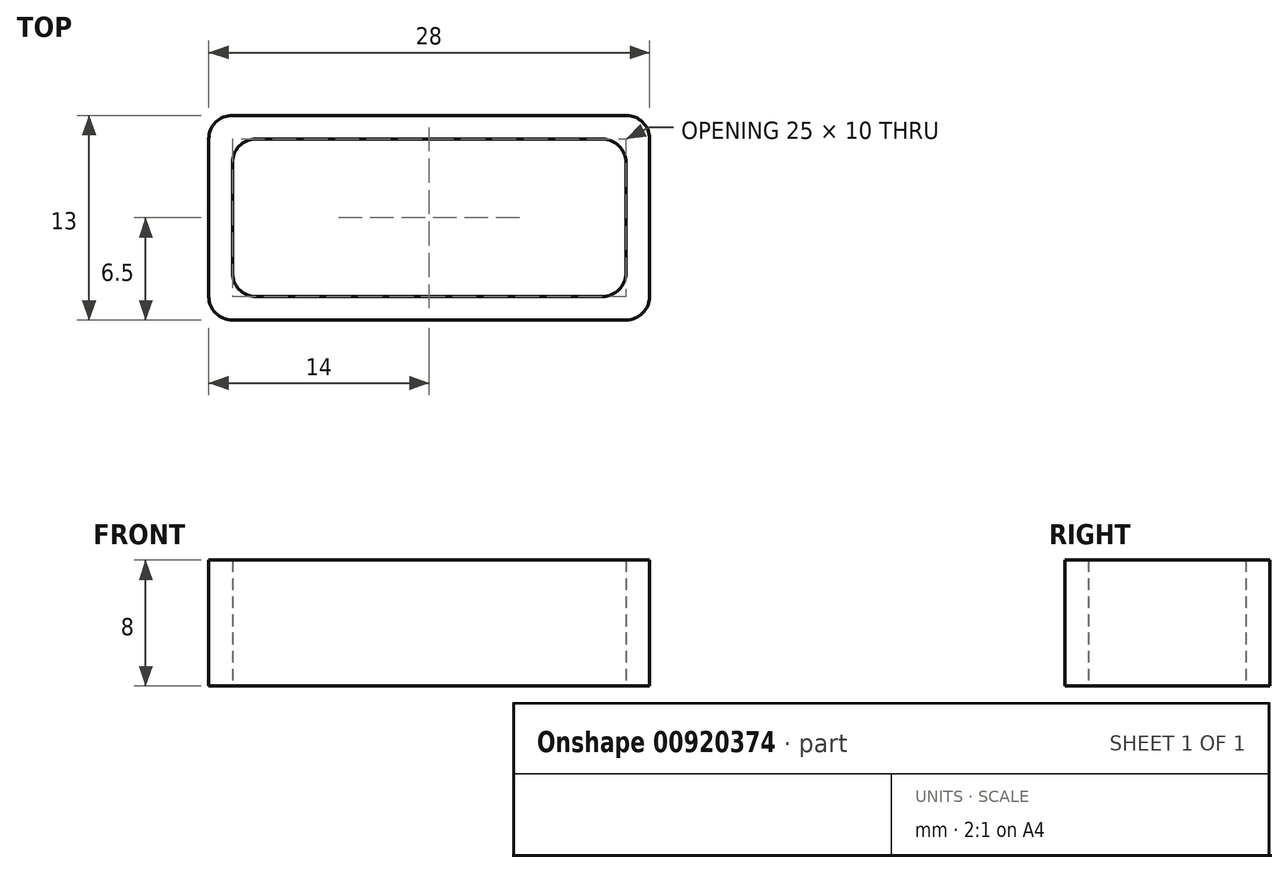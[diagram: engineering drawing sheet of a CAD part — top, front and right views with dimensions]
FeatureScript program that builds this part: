
annotation { "Feature Type Name" : "Feature", "Feature Type Description" : "" }
export const myFeature = defineFeature(function(context is Context, id is Id, definition is map)
    precondition{}
    {
        {
            var Q0;
            Q0=qCreatedBy(makeId("Top.planeOp"),FACE);
            var sketch = newSketch(context, id + "F0", { "sketchPlane" : qUnion([Q0])});
            skLineSegment(sketch, "E0.bottom", {"start": v(14, 6.5) * mm, "end": v(-14, 6.5) * mm});
            skLineSegment(sketch, "E0.top", {"start": v(14, -6.5) * mm, "end": v(-14, -6.5) * mm});
            skLineSegment(sketch, "E0.left", {"start": v(14, 6.5) * mm, "end": v(14, -6.5) * mm});
            skLineSegment(sketch, "E0.right", {"start": v(-14, 6.5) * mm, "end": v(-14, -6.5) * mm});
            skPoint(sketch, "E0.middle", {"position": v(0, 0) * mm});
            skLineSegment(sketch, "E1.bottom", {"start": v(12.5, 5) * mm, "end": v(-12.5, 5) * mm});
            skLineSegment(sketch, "E1.top", {"start": v(12.5, -5) * mm, "end": v(-12.5, -5) * mm});
            skLineSegment(sketch, "E1.left", {"start": v(12.5, 5) * mm, "end": v(12.5, -5) * mm});
            skLineSegment(sketch, "E1.right", {"start": v(-12.5, 5) * mm, "end": v(-12.5, -5) * mm});
            skSolve(sketch);
        }
        {
            var Q0;
            Q0=makeQuery(id+"F0.imprint","IMPRINT",FACE,{"disambiguationData":[TD([[makeQuery(id+"F0.imprint","IMPRINT",EDGE,{"derivedFrom":sQuery(id+"F0.wireOp",EDGE,"E0.bottom")}),1.0]])]});
            extrude(context, id + "F1", {"entities" : qUnion([Q0]), "depth" : 8 * mm, "offsetDistance" : 25 * mm});
        }
        {
            var Q0;
            Q0=makeQuery(id+"F1.opExtrude","SWEPT_EDGE",EDGE,{"disambiguationData":[OSD([sQuery(id+"F0.wireOp",EDGE,"E1.bottom"),sQuery(id+"F0.wireOp",EDGE,"E1.left")])]});
            var Q1;
            Q1=makeQuery(id+"F1.opExtrude","SWEPT_EDGE",EDGE,{"disambiguationData":[OSD([sQuery(id+"F0.wireOp",EDGE,"E1.bottom"),sQuery(id+"F0.wireOp",EDGE,"E1.right")])]});
            var Q2;
            Q2=makeQuery(id+"F1.opExtrude","SWEPT_EDGE",EDGE,{"disambiguationData":[OSD([sQuery(id+"F0.wireOp",EDGE,"E1.top"),sQuery(id+"F0.wireOp",EDGE,"E1.left")])]});
            var Q3;
            Q3=makeQuery(id+"F1.opExtrude","SWEPT_EDGE",EDGE,{"disambiguationData":[OSD([sQuery(id+"F0.wireOp",EDGE,"E1.top"),sQuery(id+"F0.wireOp",EDGE,"E1.right")])]});
            var Q4;
            Q4=makeQuery(id+"F1.opExtrude","SWEPT_EDGE",EDGE,{"disambiguationData":[OSD([sQuery(id+"F0.wireOp",EDGE,"E0.bottom"),sQuery(id+"F0.wireOp",EDGE,"E0.left")])]});
            var Q5;
            Q5=makeQuery(id+"F1.opExtrude","SWEPT_EDGE",EDGE,{"disambiguationData":[OSD([sQuery(id+"F0.wireOp",EDGE,"E0.top"),sQuery(id+"F0.wireOp",EDGE,"E0.left")])]});
            var Q6;
            Q6=makeQuery(id+"F1.opExtrude","SWEPT_EDGE",EDGE,{"disambiguationData":[OSD([sQuery(id+"F0.wireOp",EDGE,"E0.bottom"),sQuery(id+"F0.wireOp",EDGE,"E0.right")])]});
            var Q7;
            Q7=makeQuery(id+"F1.opExtrude","SWEPT_EDGE",EDGE,{"disambiguationData":[OSD([sQuery(id+"F0.wireOp",EDGE,"E0.top"),sQuery(id+"F0.wireOp",EDGE,"E0.right")])]});
            fillet(context, id + "F2", {"entities" : qUnion([Q0, Q1, Q2, Q3, Q4, Q5, Q6, Q7]), "radius" : 1.5 * mm, "tangentPropagation" : true, "allowEdgeOverflow" : false});
        }
    });
